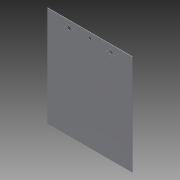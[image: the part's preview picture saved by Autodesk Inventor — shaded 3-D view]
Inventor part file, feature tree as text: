
AUTODESK INVENTOR PART (.ipt)
format: ipt  version: 2014 SP1 (Build 180222100, 222)  size: 118,272 bytes
history: native  units: mm
features: extrude x1, sketch x1
ambient origin geometry x8: Origin, YZ Plane, XZ Plane, XY Plane, X Axis, Y Axis, Z Axis, Center Point
bodies: Body1 (feature_tree)
feature tree (2):
  extrude  "Extrusion5"  Depth=360.0mm
  sketch  "Sketch9"  dims[d22=304.8mm d23=360.0mm d24=19.0mm d25=10.0mm d27=12.0mm d28=12.0mm d30=28.0mm d31=4.0mm d32=4.0mm d33=4.0mm d34=4.0mm d35=75.0mm d36=11.0mm d37=77.4mm d38=25.0mm d39=28.0mm d40=4.0mm d41=4.0mm d42=4.0mm d43=4.0mm d44=11.0mm d45=1.5875mm d46=0.0mm]
